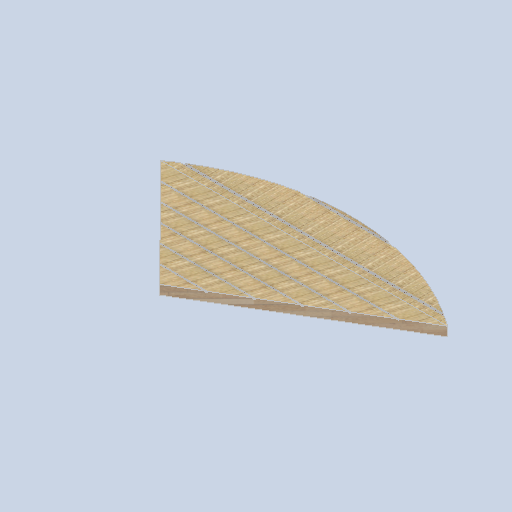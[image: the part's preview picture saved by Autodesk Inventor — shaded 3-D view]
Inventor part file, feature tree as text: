
AUTODESK INVENTOR PART (.ipt)
format: ipt  version: 2024.2 (Build 282272000, 272)  size: 438,272 bytes
history: native  units: mm
features: sketch x14, loft x6, plane x4, extrude x2
ambient origin geometry x8: Origin, YZ Plane, XZ Plane, XY Plane, X Axis, Y Axis, Z Axis, Center Point
bodies: Solid1 (feature_tree)
feature tree (26):
  sketch  "Sketch1"  dims[d0=90.0deg d1=90.0deg d2=100.0mm d3=0.0mm]
  plane  "Work Plane1"
  plane  "Work Plane2"
  plane  "Work Plane3"
  extrude  "Extrusion1"  Depth=100.0mm TaperAngle=0.0deg
  loft  "Loft1"
  loft  "Loft2"
  loft  "Loft3"
  loft  "Loft4"
  loft  "Loft5"
  loft  "Loft6"
  plane  "Work Plane4"
  extrude  "Extrusion2"  TaperAngle=0.0deg  [1 undecoded]
  sketch  "Sketch2"  dims[d4=1.745329mm d5=1.745329mm]
  sketch  "Sketch4"  dims[d6=0.0mm d7=90.0deg d8=0.0mm d9=90.0deg]
  sketch  "Sketch5"  dims[d12=0.0mm d13=90.0deg d14=0.0mm d15=90.0deg]
  sketch  "Sketch6"  dims[d18=0.0mm d19=90.0deg d20=0.0mm d21=90.0deg]
  sketch  "Sketch8"  dims[d24=0.0mm d25=90.0deg d26=0.0mm d27=90.0deg]
  sketch  "Sketch10"  dims[d30=0.0mm d31=90.0deg d32=0.0mm d33=90.0deg]
  sketch  "Sketch11"  dims[d36=0.0mm d37=90.0deg d38=0.0mm d39=90.0deg]
  sketch  "Sketch12"  dims[d40=135.0deg]
  sketch  "Sketch13"  dims[d41=3091.0mm d42=0.0mm]
  sketch  "Sketch14"
  sketch  "Sketch15"
  sketch  "Sketch16"
  sketch  "Sketch17"
note: 1 required parameter value undecoded (feature->parameter linkage not recoverable at this tier; creation-order binding heuristic only, values carry confidence <= 0.55)
